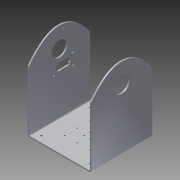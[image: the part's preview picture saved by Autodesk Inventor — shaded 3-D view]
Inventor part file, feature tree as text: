
AUTODESK INVENTOR PART (.ipt)
format: ipt  version: 2015 (Build 190159000, 159)  size: 512,512 bytes
history: native  units: in
note: dims shown in document units (in); Inventor stores cm internally (conversion verified against a paired STEP export)
features: sketch x7, other x6, sheet_metal_op x4, hole x3, chamfer x1, extrude x1, projected_geometry x1
ambient origin geometry x8: Origin, YZ Plane, XZ Plane, XY Plane, X Axis, Y Axis, Z Axis, Center Point
bodies: Body1 (feature_tree)
feature tree (23):
  sheet_metal_op  "Face2"
  sheet_metal_op  "Flange2"
  chamfer  "Corner Round1"
  hole  "Hole1"  [1 undecoded]
  sketch  "Sketch8"  dims[d193=0.0703in]
  hole  "Hole2"  [1 undecoded]
  hole  "Hole3"  [1 undecoded]
  extrude  "Extrusion1"  Depth=0.0703in
  other  "A-Side Definition"
  sketch  "Sketch3"  dims[d174=0.125in d185=6.25in]
  other  "Plate3"
  sketch  "Sketch4"  dims[d186=6.0in d187=0.0703in]
  other  "Plate4"
  sheet_metal_op  "Bend2"
  sheet_metal_op  "Corner2"
  sketch  "Sketch5"  dims[d188=0.0703in d189=0.0703in]
  sketch  "Sketch6"  dims[d190=0.0703in d191=0.0703in]
  sketch  "Sketch7"  dims[d192=0.0703in]
  sketch  "Sketch9"  dims[d194=0.072in d195=0.072in d196=0.0703in d197=0.0703in d198=0.0703in d199=0.072in d200=0.072in d201=0.0703in d202=0.0703in d203=0.072in d204=0.0703in d205=1.97in d206=1.97in d207=0.25in d208=0.25in d209=0.0703in d210=0.072in d211=0.0703in d212=0.0703in d213=0.072in d214=0.072in d215=0.0703in d216=0.0703in d217=0.0703in d218=0.072in d219=0.0703in d220=0.0703in d221=0.0703in d222=0.0703in d223=0.0703in d224=0.0703in d225=2.9297in d226=1.375in d227=3.0in d228=3.0in d229=2.9297in d230=1.875in d231=3.0in d232=3.0in d233=1.6922in d234=1.8876in d235=1.7626in d236=1.7626in d237=4.1671in d238=1.8876in d239=4.2374in d240=4.2374in d241=2.0458in d242=2.2411in d243=2.1161in d244=2.1161in d245=3.8136in d246=2.2411in d247=3.8839in d248=3.8839in d249=2.928in d250=2.375in d251=3.0in d252=3.0in d253=2.3994in d254=2.5947in d255=2.4697in d256=2.4697in d257=3.46in d258=2.5947in d259=3.5303in d260=3.5303in d261=2.9297in d262=2.74in d263=3.0in d264=3.0in d265=2.6558in d266=2.8528in d267=2.7278in d268=2.7278in d269=3.2002in d270=2.8528in d271=3.2722in d272=3.2722in d273=1.03in d274=3.125in d275=1.1797in d276=3.125in d277=1.25in d278=1.25in d279=1.6797in d280=3.125in d281=1.75in d282=1.75in d283=2.178in d284=3.125in d285=2.25in d286=2.25in d287=2.5447in d288=3.125in d289=2.615in d290=2.615in d291=2.75in d292=3.125in d293=3.0in d294=3.0in d295=3.3147in d296=3.125in d297=3.385in d298=3.385in d299=3.678in d300=3.125in d301=3.75in d302=3.75in d303=4.1797in d304=3.125in d305=4.25in d306=4.25in d307=4.6797in d308=3.125in d309=4.75in d310=4.75in d311=2.6558in d312=3.3972in d313=2.7278in d314=2.7278in d315=3.2002in d316=3.3972in d317=3.2722in d318=3.2722in d319=2.9297in d320=3.51in d321=3.0in d322=3.0in d323=2.3994in d324=3.6553in d325=2.4697in d326=2.4697in d327=3.46in d328=3.6553in d329=3.5303in d330=3.5303in d331=2.928in d332=3.875in d333=3.0in d334=3.0in d335=2.0458in d336=4.0089in d337=2.1161in d338=2.1161in d339=3.8136in d340=4.0089in d341=3.8839in d342=3.8839in d343=1.6922in d344=4.3624in d345=1.7626in d346=1.7626in d347=4.1671in d348=4.3624in d349=4.2374in d350=4.2374in d351=2.9297in d352=4.375in d353=3.0in d354=3.0in d355=2.9297in d356=4.875in d357=3.0in d358=3.0in d359=0.125in d360=0.125in d361=0.0625in d362=0.25in d363=0.125in d364=8.0in d365=90.0deg d366=0.125in d367=0.5in d368=0.125in d369=0.125in d370=6.0in d371=2.0in d372=1.5in d373=0.125in d374=0.0in d375=0.25in d376=2.9736in d377=2.9736in d378=0.094in d379=0.094in d380=0.094in d381=0.094in d382=0.094in d383=0.094in d384=0.094in d385=0.094in d386=6.063in d387=6.063in d388=3.0315in d389=3.0315in d390=2.383in d391=2.383in d392=2.383in d393=2.383in d394=2.383in d395=2.383in d396=2.383in d397=2.383in d398=4.6195in d399=0.711in d400=5.477in d401=0.711in d402=5.477in d403=0.19in d404=0.75in d405=0.375in d406=0.25in d407=0.5635in d408=0.125in d409=0.8108in d410=0.732in d411=1.5in d412=0.489in d413=0.8268in d414=0.3494in d415=0.3494in d416=0.1517in d417=0.125in d418=0.0in d419=0.144in d420=0.75in d421=0.279in d422=0.25in d423=0.5635in d424=0.125in d425=0.8108in d426=0.104in d427=0.276in d428=0.279in d429=0.25in d430=0.5635in d431=0.432in d432=0.8108in d433=1.0in d434=0.0in]
  projected_geometry  "Projected Loop1"
  other  "Cut1"
  other  "Cut2"
  other  "Definition1"
note: 3 required parameter values undecoded (feature->parameter linkage not recoverable at this tier; creation-order binding heuristic only, values carry confidence <= 0.55)
